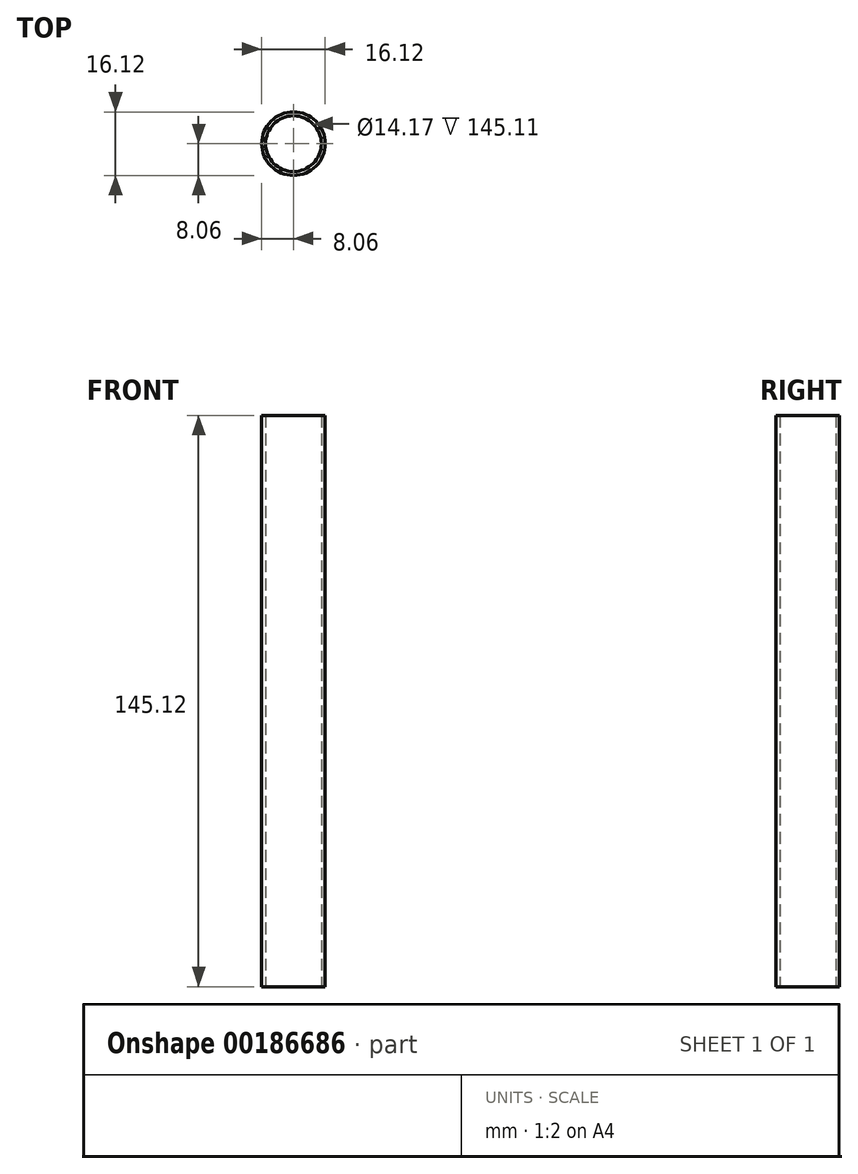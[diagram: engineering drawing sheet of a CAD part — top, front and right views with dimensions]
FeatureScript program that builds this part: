
annotation { "Feature Type Name" : "Feature", "Feature Type Description" : "" }
export const myFeature = defineFeature(function(context is Context, id is Id, definition is map)
    precondition{}
    {
        {
            var Q0;
            Q0=qCreatedBy(makeId("Top.planeOp"),FACE);
            var sketch = newSketch(context, id + "F0", { "sketchPlane" : qUnion([Q0])});
            skCircle(sketch, "E0", {"center": v(0, 0) * mm, "radius": 8.06 * mm});
            skSolve(sketch);
        }
        {
            var Q0;
            Q0=makeQuery(id+"F0.imprint","IMPRINT",FACE,{"disambiguationData":[TD([[makeQuery(id+"F0.imprint","IMPRINT",EDGE,{"derivedFrom":sQuery(id+"F0.wireOp",EDGE,"E0")}),1.0]])]});
            extrude(context, id + "F1", {"entities" : qUnion([Q0]), "depth" : 72.56 * mm});
        }
        {
            var Q0;
            Q0=makeQuery(id+"F0.imprint","IMPRINT",FACE,{"disambiguationData":[TD([[makeQuery(id+"F0.imprint","IMPRINT",EDGE,{"derivedFrom":sQuery(id+"F0.wireOp",EDGE,"E0")}),1.0]])]});
            extrude(context, id + "F2", {"entities" : qUnion([Q0]), "operationType" : NewBodyOperationType.ADD, "oppositeDirection" : true, "depth" : 72.56 * mm});
        }
        {
            var Q0;
            Q0 = qSketchRegion(id + "F0", true);
            extrude(context, id + "F3", {"entities" : qUnion([Q0]), "operationType" : NewBodyOperationType.ADD, "depth" : 25.4 * mm});
        }
        {
            var Q0;
            Q0=makeQuery(id+"F2.opExtrude","CAP_FACE",FACE,{"disambiguationData":[OSD([sQuery(id+"F0.wireOp",EDGE,"E0")])],"isStart":false});
            var sketch = newSketch(context, id + "F4", { "sketchPlane" : qUnion([Q0])});
            skCircle(sketch, "E1", {"center": v(0, 0) * mm, "radius": 7.09 * mm});
            skLineSegment(sketch, "E2", {"start": v(0, 7.09) * mm, "end": v(0, -7.09) * mm});
            skSolve(sketch);
        }
        {
            var Q0;
            {var subQ0=sQuery(id+"F4.wireOp",EDGE,"E2");Q0=makeQuery(id+"F4.imprint","IMPRINT",FACE,{"disambiguationData":[TD([[makeQuery(id+"F4.imprint","IMPRINT",EDGE,{"derivedFrom":subQ0}),-1.0]])]});}
            var Q1;
            {var subQ0=sQuery(id+"F4.wireOp",EDGE,"E2");Q1=makeQuery(id+"F4.imprint","IMPRINT",FACE,{"disambiguationData":[TD([[makeQuery(id+"F4.imprint","IMPRINT",EDGE,{"derivedFrom":subQ0}),1.0]])]});}
            extrude(context, id + "F5", {"entities" : qUnion([Q0, Q1]), "operationType" : NewBodyOperationType.REMOVE, "oppositeDirection" : true, "depth" : 145.11 * mm});
        }
    });
